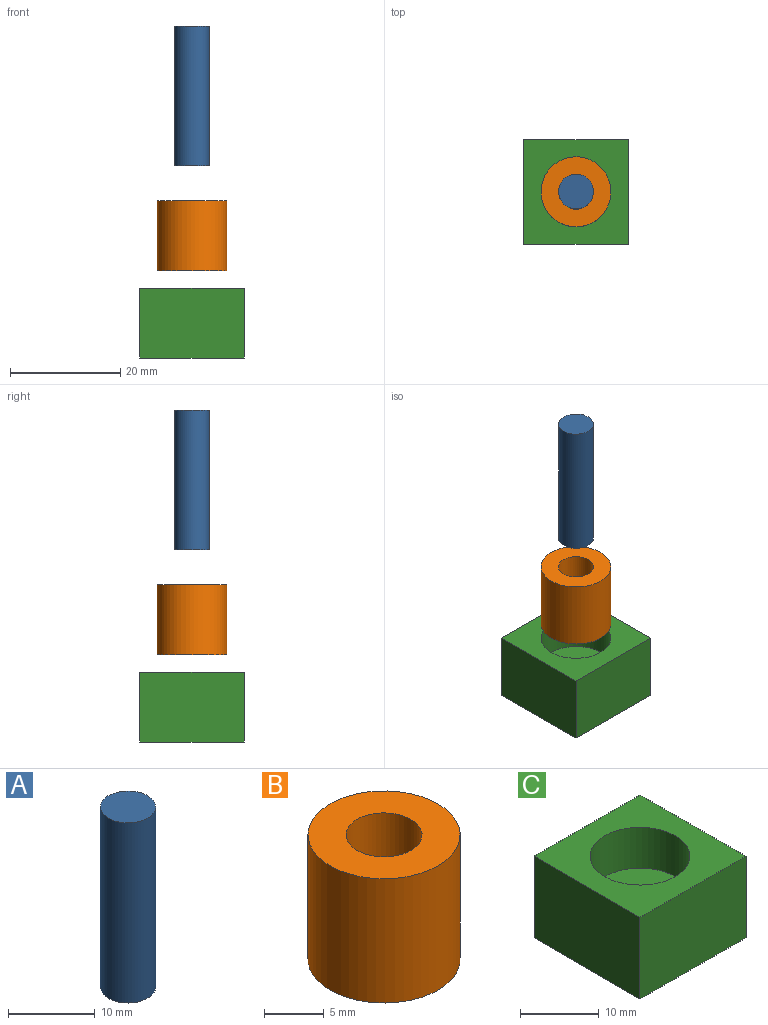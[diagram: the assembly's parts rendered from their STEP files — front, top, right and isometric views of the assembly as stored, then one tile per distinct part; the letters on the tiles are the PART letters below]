
ASSEMBLY  parts=3 mates=2
PART A: 3 faces, bbox 6.4x6.4x25.4 mm
  f0: cylinder r=3.17mm len=25.4mm, axis (0,0,-1), area 506.7mm2, adj f1,f2
  f1: plane 6.35x6.35mm, normal (0,0,1), area 31.7mm2, adj f0
  f2: plane 6.35x6.35mm, normal (0,0,-1), area 31.7mm2, adj f0
PART B: 4 faces, bbox 12.7x12.7x12.7 mm
  f0: cylinder r=3.17mm len=12.7mm, axis (0,0,-1), area 253.4mm2, adj f2,f3
  f1: cylinder r=6.35mm len=12.7mm, axis (0,0,-1), area 506.7mm2, adj f2,f3
  f2: plane 12.7x12.7mm, normal (0,0,1), area 95mm2, adj f0,f1
  f3: plane 12.7x12.7mm, normal (0,0,-1), area 95mm2, adj f0,f1
PART C: 8 faces, bbox 19.1x19.1x12.7 mm
  f0: plane 19.05x12.7mm, normal (1,0,0), area 241.9mm2, adj f1,f3,f4,f5
  f1: plane 19.05x12.7mm, normal (0,1,0), area 241.9mm2, adj f0,f2,f4,f5
  f2: plane 19.05x12.7mm, normal (-1,0,0), area 241.9mm2, adj f1,f3,f4,f5
  f3: plane 19.05x12.7mm, normal (0,-1,0), area 241.9mm2, adj f0,f2,f4,f5
  f4: plane 19.05x19.05mm, normal (0,0,1), area 236.2mm2, adj f0,f1,f2,f3,f6
  f5: plane 19.05x19.05mm, normal (0,0,-1), area 362.9mm2, adj f0,f1,f2,f3
  f6: cylinder r=6.35mm len=12.7mm, axis (0,0,1), area 253.4mm2, adj f4,f7
  f7: plane 12.7x12.7mm, normal (0,0,1), area 126.7mm2, adj f6
PLACE A rot(axis=(1,0,0),180deg) t=(0,0,60.32)mm
PLACE B rot(axis=(1,0,0),180deg) t=(0,0,28.58)mm
PLACE C at identity fixed
MATE fastened A.f0 <-> C.f6  axis (0,0,1) through (0,0,60.32)mm
MATE fastened B.f0 <-> C.f6  axis (0,0,1) through (0,0,28.58)mm
